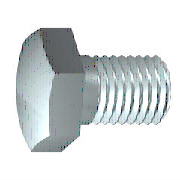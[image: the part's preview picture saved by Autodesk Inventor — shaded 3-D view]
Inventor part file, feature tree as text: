
AUTODESK INVENTOR PART (.ipt)
format: ipt  version: 2013 (Build 170138000, 138)  size: 183,296 bytes
history: native  units: mm (DEFAULTED — no unit token found)
features: sketch x2, extrude x1, chamfer x1, plane x1
ambient origin geometry x7: Origin, YZ Plane, XZ Plane, X Axis, Y Axis, Z Axis, Center Point
bodies: Solid1 (feature_tree), Body (feature_tree)
feature tree (5):
  extrude  "Head"  TaperAngle=90.0deg  [1 undecoded]
  chamfer  "Chamfer1"  [1 undecoded]
  plane  "Work Plane1"
  sketch  "Sketch1"  dims[d2=8.0mm d12=90.0deg]
  sketch  "Sketch2"  dims[d3=5.68mm d4=0.0mm d21=90.0deg d6=0.766813mm d7=0.766912mm d8=0.0mm d11=13.0mm d15=22.0mm d16=0.0mm d55=45.0deg d58=0.0mm d59=100.0mm d65=13.0mm d67=30.0deg d68=15.6mm d69=5.68mm d71=0.1mm d73=0.0mm]
note: 2 required parameter values undecoded (feature->parameter linkage not recoverable at this tier; creation-order binding heuristic only, values carry confidence <= 0.55)
